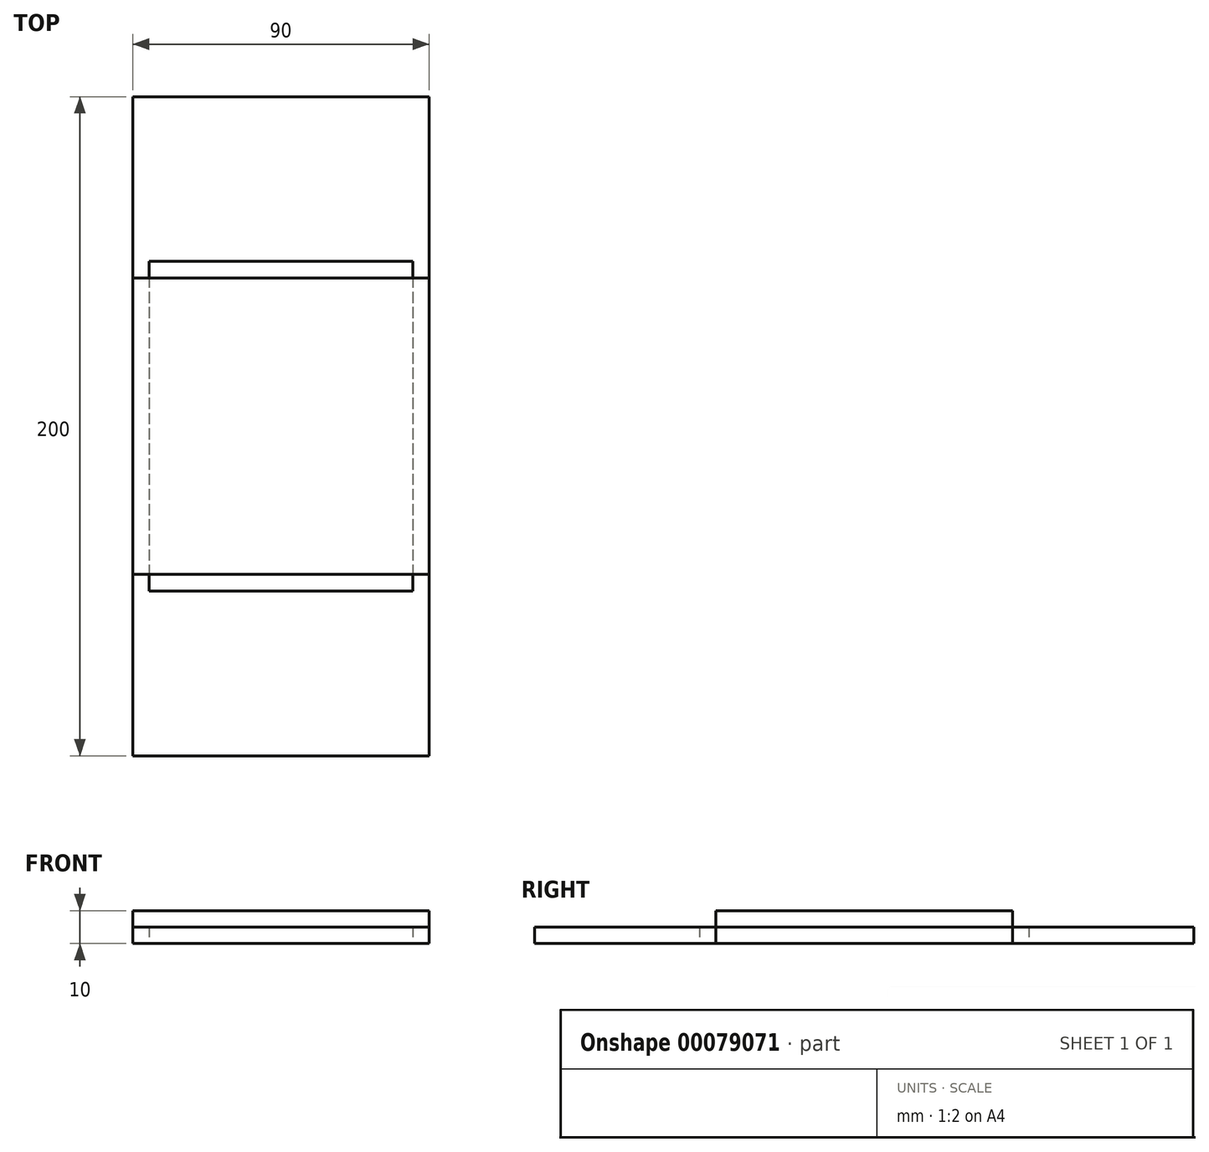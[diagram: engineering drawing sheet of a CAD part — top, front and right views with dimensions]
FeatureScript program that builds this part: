
annotation { "Feature Type Name" : "Feature", "Feature Type Description" : "" }
export const myFeature = defineFeature(function(context is Context, id is Id, definition is map)
    precondition{}
    {
        {
            var Q0;
            Q0=qCreatedBy(makeId("Top.planeOp"),FACE);
            var sketch = newSketch(context, id + "F0", { "sketchPlane" : qUnion([Q0])});
            skLineSegment(sketch, "E0.bottom", {"start": v(45, 45) * mm, "end": v(-45, 45) * mm});
            skLineSegment(sketch, "E0.top", {"start": v(45, -45) * mm, "end": v(-45, -45) * mm});
            skLineSegment(sketch, "E0.left", {"start": v(45, 45) * mm, "end": v(45, -45) * mm});
            skLineSegment(sketch, "E0.right", {"start": v(-45, 45) * mm, "end": v(-45, -45) * mm});
            skPoint(sketch, "E0.middle", {"position": v(0, 0) * mm});
            skSolve(sketch);
        }
        {
            var Q0;
            Q0=qCreatedBy(makeId("Top.planeOp"),FACE);
            var sketch = newSketch(context, id + "F1", { "sketchPlane" : qUnion([Q0])});
            skLineSegment(sketch, "E1.bottom", {"start": v(40, 50) * mm, "end": v(-40, 50) * mm});
            skLineSegment(sketch, "E1.top", {"start": v(40, -50) * mm, "end": v(-40, -50) * mm});
            skLineSegment(sketch, "E1.left", {"start": v(40, 50) * mm, "end": v(40, -50) * mm});
            skLineSegment(sketch, "E1.right", {"start": v(-40, 50) * mm, "end": v(-40, -50) * mm});
            skPoint(sketch, "E1.middle", {"position": v(0, 0) * mm});
            skSolve(sketch);
        }
        {
            var Q0;
            Q0=qCreatedBy(makeId("Top.planeOp"),FACE);
            var sketch = newSketch(context, id + "F2", { "sketchPlane" : qUnion([Q0])});
            skLineSegment(sketch, "E2.bottom", {"start": v(45, 100) * mm, "end": v(-45, 100) * mm});
            skLineSegment(sketch, "E2.top", {"start": v(45, -100) * mm, "end": v(-45, -100) * mm});
            skLineSegment(sketch, "E2.left", {"start": v(45, 100) * mm, "end": v(45, -100) * mm});
            skLineSegment(sketch, "E2.right", {"start": v(-45, 100) * mm, "end": v(-45, -100) * mm});
            skPoint(sketch, "E2.middle", {"position": v(0, 0) * mm});
            skSolve(sketch);
        }
        {
            var Q0;
            Q0 = qSketchRegion(id + "F0", true);
            extrude(context, id + "F3", {"entities" : qUnion([Q0]), "depth" : 10 * mm});
        }
        {
            var Q0;
            Q0 = qSketchRegion(id + "F1", true);
            extrude(context, id + "F4", {"entities" : qUnion([Q0]), "depth" : 5 * mm});
        }
        {
            var Q0;
            Q0 = qSketchRegion(id + "F2", true);
            extrude(context, id + "F5", {"entities" : qUnion([Q0]), "depth" : 5 * mm});
        }
    });
